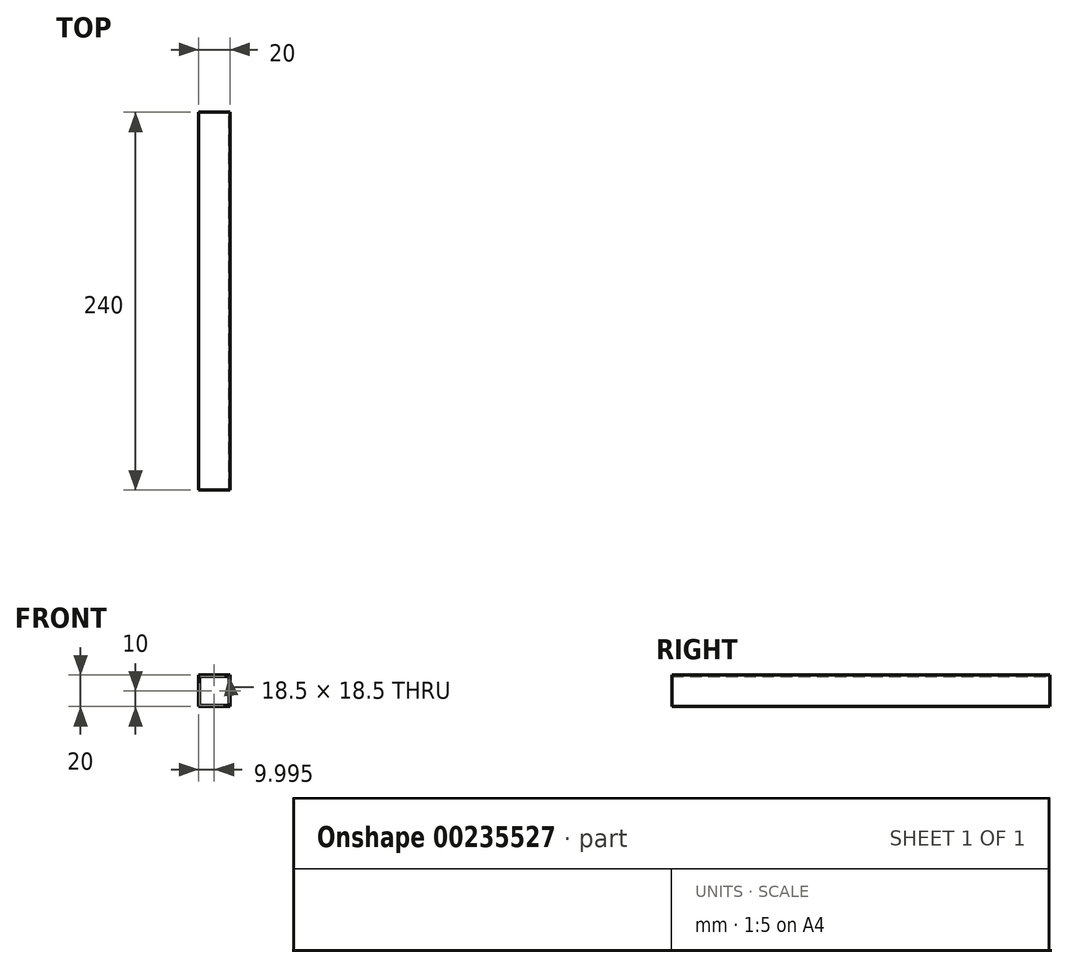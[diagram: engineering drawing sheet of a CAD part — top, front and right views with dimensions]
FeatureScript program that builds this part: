
annotation { "Feature Type Name" : "Feature", "Feature Type Description" : "" }
export const myFeature = defineFeature(function(context is Context, id is Id, definition is map)
    precondition{}
    {
        {
            var Q0;
            Q0=qCreatedBy(makeId("Front.planeOp"),FACE);
            var sketch = newSketch(context, id + "F0", { "sketchPlane" : qUnion([Q0])});
            skLineSegment(sketch, "E0.bottom", {"start": v(-34.48, 27) * mm, "end": v(-54.48, 27) * mm});
            skLineSegment(sketch, "E0.top", {"start": v(-34.48, 47) * mm, "end": v(-54.48, 47) * mm});
            skLineSegment(sketch, "E0.left", {"start": v(-34.48, 27) * mm, "end": v(-34.48, 47) * mm});
            skLineSegment(sketch, "E0.right", {"start": v(-54.48, 27) * mm, "end": v(-54.48, 47) * mm});
            skPoint(sketch, "E0.middle", {"position": v(-44.48, 37) * mm});
            skLineSegment(sketch, "E1.bottom", {"start": v(-35.23, 27.75) * mm, "end": v(-53.73, 27.75) * mm});
            skLineSegment(sketch, "E1.top", {"start": v(-35.23, 46.25) * mm, "end": v(-53.73, 46.25) * mm});
            skLineSegment(sketch, "E1.left", {"start": v(-35.23, 27.75) * mm, "end": v(-35.23, 46.25) * mm});
            skLineSegment(sketch, "E1.right", {"start": v(-53.73, 27.75) * mm, "end": v(-53.73, 46.25) * mm});
            skSolve(sketch);
        }
        {
            var Q0;
            Q0=makeQuery(id+"F0.imprint","IMPRINT",FACE,{"disambiguationData":[TD([[makeQuery(id+"F0.imprint","IMPRINT",EDGE,{"derivedFrom":sQuery(id+"F0.wireOp",EDGE,"E0.bottom")}),-1.0]])]});
            extrude(context, id + "F1", {"entities" : qUnion([Q0]), "depth" : 240 * mm});
        }
    });
